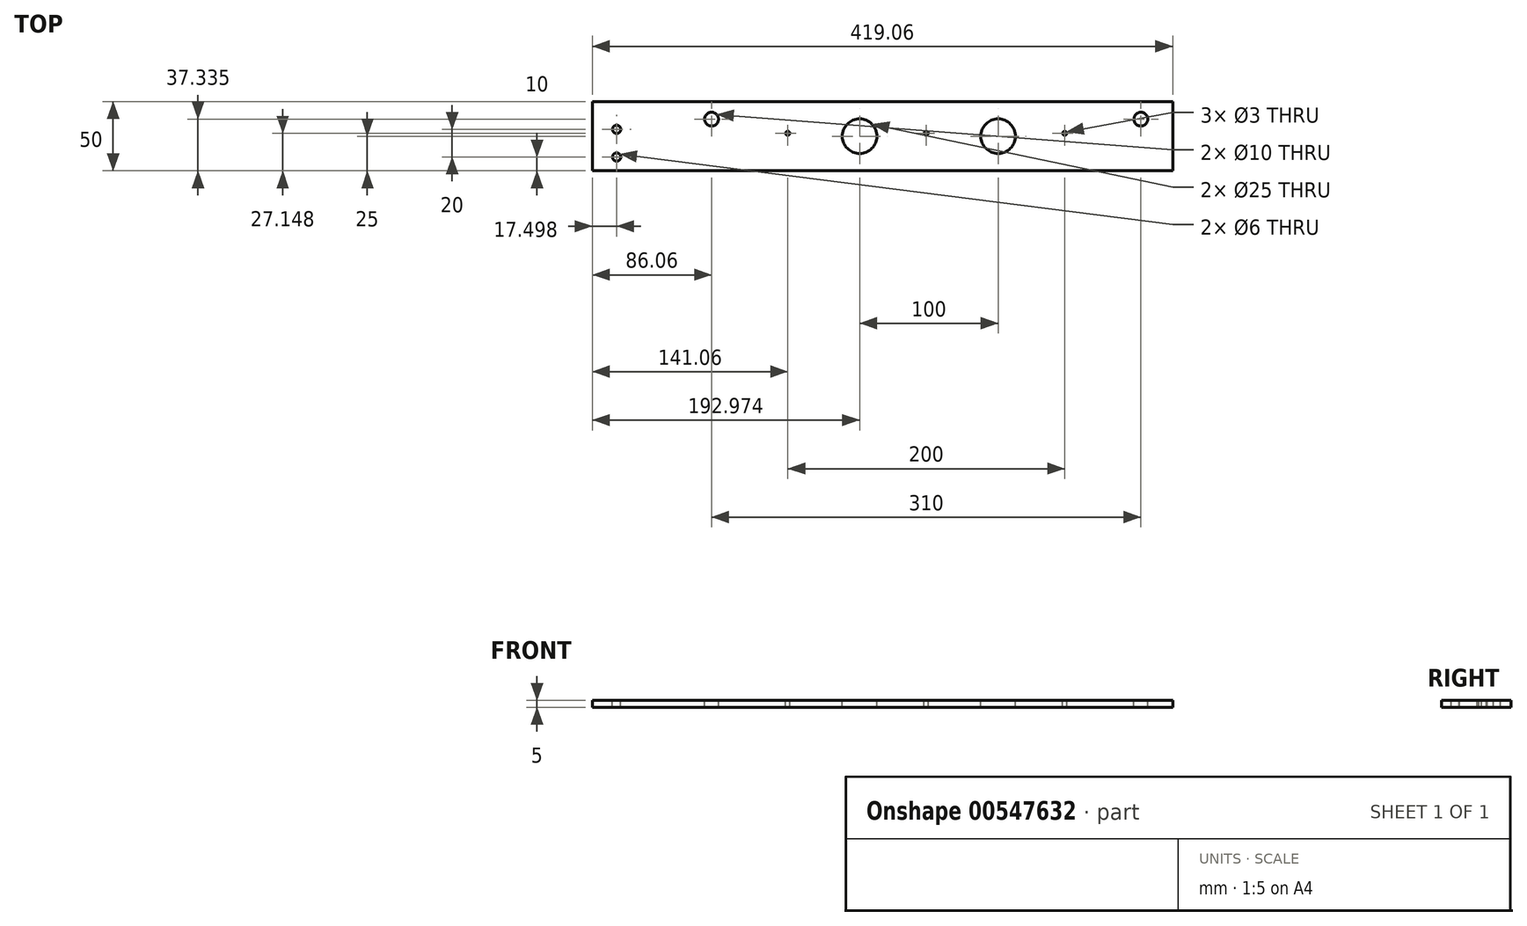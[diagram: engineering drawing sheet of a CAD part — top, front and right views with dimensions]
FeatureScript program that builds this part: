
annotation { "Feature Type Name" : "Feature", "Feature Type Description" : "" }
export const myFeature = defineFeature(function(context is Context, id is Id, definition is map)
    precondition{}
    {
        {
            var Q0;
            Q0=qCreatedBy(makeId("Top.planeOp"),FACE);
            var sketch = newSketch(context, id + "F0", { "sketchPlane" : qUnion([Q0])});
            skLineSegment(sketch, "E0.bottom", {"start": v(178, 25) * mm, "end": v(-178, 25) * mm});
            skLineSegment(sketch, "E0.top", {"start": v(178, -25) * mm, "end": v(-178, -25) * mm});
            skLineSegment(sketch, "E0.left", {"start": v(178, 25) * mm, "end": v(178, -25) * mm});
            skLineSegment(sketch, "E0.right", {"start": v(-178, 25) * mm, "end": v(-178, -25) * mm});
            skPoint(sketch, "E0.middle", {"position": v(0, 0) * mm});
            skSolve(sketch);
        }
        {
            var Q0;
            Q0=makeQuery(id+"F0.imprint","IMPRINT",FACE,{"disambiguationData":[TD([[makeQuery(id+"F0.imprint","IMPRINT",EDGE,{"derivedFrom":sQuery(id+"F0.wireOp",EDGE,"E0.bottom")}),1.0]])]});
            extrude(context, id + "F1", {"entities" : qUnion([Q0]), "depth" : 5 * mm, "offsetDistance" : 25 * mm});
        }
        {
            var Q0;
            Q0=makeQuery(id+"F1.opExtrude","CAP_FACE",FACE,{"disambiguationData":[OSD([sQuery(id+"F0.wireOp",EDGE,"E0.bottom"),sQuery(id+"F0.wireOp",EDGE,"E0.top"),sQuery(id+"F0.wireOp",EDGE,"E0.left"),sQuery(id+"F0.wireOp",EDGE,"E0.right")])],"isStart":false});
            var sketch = newSketch(context, id + "F2", { "sketchPlane" : qUnion([Q0])});
            skCircle(sketch, "E1", {"center": v(-155, 12.34) * mm, "radius": 5 * mm});
            skCircle(sketch, "E2", {"center": v(155, 12.34) * mm, "radius": 5 * mm});
            skLineSegment(sketch, "E3", {"start": v(-155, 12.34) * mm, "end": v(155, 12.34) * mm, "construction": true});
            skPoint(sketch, "E4", {"position": v(0, 12.34) * mm});
            skCircle(sketch, "E5", {"center": v(-48.09, 0) * mm, "radius": 12.5 * mm});
            skPoint(sketch, "E6", {"position": v(0, 0) * mm});
            skCircle(sketch, "E7", {"center": v(51.91, 0) * mm, "radius": 12.5 * mm});
            skSolve(sketch);
        }
        {
            var Q0;
            Q0 = qSketchRegion(id + "F2", true);
            extrude(context, id + "F3", {"entities" : qUnion([Q0]), "operationType" : NewBodyOperationType.REMOVE, "endBound" : BoundingType.THROUGH_ALL, "oppositeDirection" : true, "depth" : 25 * mm, "offsetDistance" : 25 * mm});
        }
        {
            var Q0;
            Q0=makeQuery(id+"F1.opExtrude","CAP_FACE",FACE,{"disambiguationData":[OSD([sQuery(id+"F0.wireOp",EDGE,"E0.bottom"),sQuery(id+"F0.wireOp",EDGE,"E0.top"),sQuery(id+"F0.wireOp",EDGE,"E0.left"),sQuery(id+"F0.wireOp",EDGE,"E0.right")])],"isStart":false});
            var sketch = newSketch(context, id + "F4", { "sketchPlane" : qUnion([Q0])});
            skCircle(sketch, "E8", {"center": v(0, 2.15) * mm, "radius": 1.5 * mm});
            skCircle(sketch, "E9", {"center": v(100, 2.15) * mm, "radius": 1.5 * mm});
            skCircle(sketch, "E10", {"center": v(-100, 2.15) * mm, "radius": 1.5 * mm});
            skLineSegment(sketch, "E11", {"start": v(-100, 2.15) * mm, "end": v(0, 2.15) * mm, "construction": true});
            skLineSegment(sketch, "E12", {"start": v(0, 2.15) * mm, "end": v(100, 2.15) * mm, "construction": true});
            skSolve(sketch);
        }
        {
            var Q0;
            Q0 = qSketchRegion(id + "F4", true);
            extrude(context, id + "F5", {"entities" : qUnion([Q0]), "operationType" : NewBodyOperationType.REMOVE, "endBound" : BoundingType.THROUGH_ALL, "oppositeDirection" : true, "depth" : 25 * mm, "offsetDistance" : 25 * mm});
        }
        {
            var Q0;
            Q0=qCreatedBy(makeId("Top.planeOp"),FACE);
            var sketch = newSketch(context, id + "F6", { "sketchPlane" : qUnion([Q0])});
            skLineSegment(sketch, "E13.bottom", {"start": v(61.73, 58.93) * mm, "end": v(12.32, 58.93) * mm});
            skLineSegment(sketch, "E13.top", {"start": v(61.73, 37.83) * mm, "end": v(12.32, 37.83) * mm});
            skLineSegment(sketch, "E13.left", {"start": v(61.73, 58.93) * mm, "end": v(61.73, 37.83) * mm});
            skLineSegment(sketch, "E13.right", {"start": v(12.32, 58.93) * mm, "end": v(12.32, 37.83) * mm});
            skPoint(sketch, "E13.middle", {"position": v(37.02, 48.38) * mm});
            skSolve(sketch);
        }
        {
            var Q0;
            Q0 = qSketchRegion(id + "F6", true);
            extrude(context, id + "F7", {"entities" : qUnion([Q0]), "depth" : 25 * mm, "offsetDistance" : 25 * mm});
        }
        {
            var Q0;
            Q0=makeQuery(id+"F7.opExtrude","SWEPT_BODY",BODY,{"disambiguationData":[OSD([sQuery(id+"F6.wireOp",EDGE,"E13.bottom"),sQuery(id+"F6.wireOp",EDGE,"E13.top"),sQuery(id+"F6.wireOp",EDGE,"E13.left"),sQuery(id+"F6.wireOp",EDGE,"E13.right")])]});
            deleteBodies(context, id + "F8", {"entities" : qUnion([Q0])});
        }
        {
            var Q0;
            Q0=qCreatedBy(makeId("Top.planeOp"),FACE);
            var sketch = newSketch(context, id + "F9", { "sketchPlane" : qUnion([Q0])});
            skLineSegment(sketch, "E14.bottom", {"start": v(-178, 25) * mm, "end": v(-241.06, 25) * mm});
            skLineSegment(sketch, "E14.top", {"start": v(-178, -25) * mm, "end": v(-241.06, -25) * mm});
            skLineSegment(sketch, "E14.left", {"start": v(-178, 25) * mm, "end": v(-178, -25) * mm});
            skLineSegment(sketch, "E14.right", {"start": v(-241.06, 25) * mm, "end": v(-241.06, -25) * mm});
            skSolve(sketch);
        }
        {
            var Q0;
            Q0 = qSketchRegion(id + "F9", true);
            var Q1;
            Q1=makeQuery(id+"F1.opExtrude","CAP_FACE",FACE,{"disambiguationData":[OSD([sQuery(id+"F0.wireOp",EDGE,"E0.bottom"),sQuery(id+"F0.wireOp",EDGE,"E0.top"),sQuery(id+"F0.wireOp",EDGE,"E0.left"),sQuery(id+"F0.wireOp",EDGE,"E0.right")])],"isStart":false});
            extrude(context, id + "F10", {"entities" : qUnion([Q0]), "operationType" : NewBodyOperationType.ADD, "endBound" : BoundingType.UP_TO_SURFACE, "depth" : 25 * mm, "endBoundEntityFace" : qUnion([Q1]), "offsetDistance" : 25 * mm});
        }
        {
            var Q0;
            {var subQ0=sQuery(id+"F0.wireOp",EDGE,"E0.right");var subQ1=sQuery(id+"F0.wireOp",EDGE,"E0.left");var subQ2=sQuery(id+"F0.wireOp",EDGE,"E0.top");var subQ3=sQuery(id+"F0.wireOp",EDGE,"E0.bottom");Q0=makeQuery(id+"F10.boolean.opBoolean","MERGE",FACE,{"derivedFrom":[makeQuery(id+"F1.opExtrude","CAP_FACE",FACE,{"disambiguationData":[OSD([subQ3,subQ2,subQ1,subQ0])],"isStart":false}),makeQuery(id+"F10.opExtrude","CAP_FACE",FACE,{"disambiguationData":[OSD([subQ3,subQ2,subQ1,subQ0])],"isStart":false})]});}
            var sketch = newSketch(context, id + "F11", { "sketchPlane" : qUnion([Q0])});
            skCircle(sketch, "E15", {"center": v(-223.56, 5) * mm, "radius": 3 * mm});
            skCircle(sketch, "E16", {"center": v(-223.56, -15) * mm, "radius": 3 * mm});
            skSolve(sketch);
        }
        {
            var Q0;
            Q0 = qSketchRegion(id + "F11", true);
            extrude(context, id + "F12", {"entities" : qUnion([Q0]), "operationType" : NewBodyOperationType.REMOVE, "oppositeDirection" : true, "depth" : 25 * mm, "offsetDistance" : 25 * mm});
        }
    });
